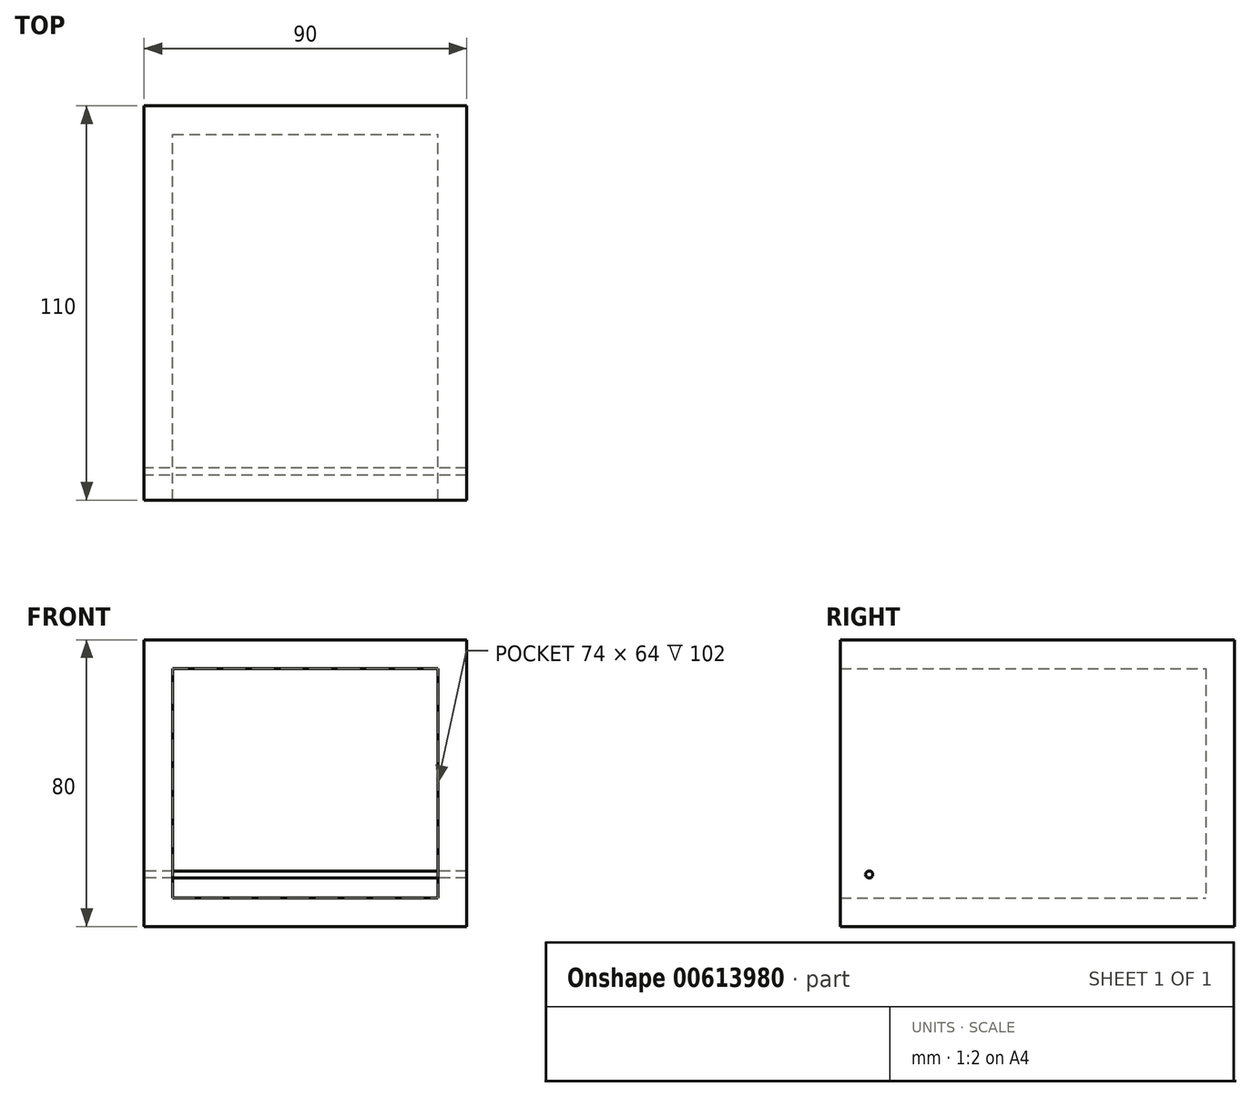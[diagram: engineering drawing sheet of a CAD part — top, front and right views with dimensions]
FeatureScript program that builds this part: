
annotation { "Feature Type Name" : "Feature", "Feature Type Description" : "" }
export const myFeature = defineFeature(function(context is Context, id is Id, definition is map)
    precondition{}
    {
        {
            var Q0;
            Q0=qCreatedBy(makeId("Top.planeOp"),FACE);
            var sketch = newSketch(context, id + "F0", { "sketchPlane" : qUnion([Q0])});
            skPoint(sketch, "E0", {"position": v(-35, 0) * mm});
            skPoint(sketch, "E1", {"position": v(-35, -40.17) * mm});
            skPoint(sketch, "E2", {"position": v(0, -40.17) * mm});
            skPoint(sketch, "E3", {"position": v(0, 61.83) * mm});
            skPoint(sketch, "E4", {"position": v(45, 61.83) * mm});
            skLineSegment(sketch, "E5", {"start": v(45, 61.83) * mm, "end": v(0, 61.83) * mm});
            skLineSegment(sketch, "E6", {"start": v(0, -40.17) * mm, "end": v(45, -40.17) * mm});
            skPoint(sketch, "E7", {"position": v(0, -48.17) * mm});
            skLineSegment(sketch, "E8", {"start": v(0, -48.17) * mm, "end": v(45, -48.17) * mm});
            skLineSegment(sketch, "E9", {"start": v(45, -48.17) * mm, "end": v(45, 61.83) * mm});
            skPoint(sketch, "E10", {"position": v(0, 55.73) * mm});
            skPoint(sketch, "E11", {"position": v(-45, 41.83) * mm});
            skLineSegment(sketch, "E12.MirrorCS", {"start": v(-45, -48.17) * mm, "end": v(-45, 61.83) * mm});
            skLineSegment(sketch, "E13.MirrorCS", {"start": v(-45, 61.83) * mm, "end": v(0, 61.83) * mm});
            skLineSegment(sketch, "E14.MirrorCS", {"start": v(0, -40.17) * mm, "end": v(-45, -40.17) * mm});
            skLineSegment(sketch, "E15.MirrorCS", {"start": v(0, -48.17) * mm, "end": v(-45, -48.17) * mm});
            skLineSegment(sketch, "E16", {"start": v(0, 61.83) * mm, "end": v(0, -48.17) * mm});
            skSolve(sketch);
        }
        {
            var Q0;
            Q0=makeQuery(id+"F0.imprint","IMPRINT",FACE,{"disambiguationData":[TD([[makeQuery(id+"F0.imprint","IMPRINT",EDGE,{"derivedFrom":sQuery(id+"F0.wireOp",EDGE,"2yOScowH-2bkr-TMic-voUo-hkF0jfRCA1gd.bottom")}),1.0]])]});
            var Q1;
            {var subQ0=sQuery(id+"F0.wireOp",EDGE,"E13.MirrorCS");Q1=makeQuery(id+"F0.imprint","IMPRINT",FACE,{"disambiguationData":[TD([[makeQuery(id+"F0.imprint","IMPRINT",EDGE,{"derivedFrom":subQ0}),-1.0]])]});}
            var Q2;
            {var subQ0=sQuery(id+"F0.wireOp",EDGE,"E5");Q2=makeQuery(id+"F0.imprint","IMPRINT",FACE,{"disambiguationData":[TD([[makeQuery(id+"F0.imprint","IMPRINT",EDGE,{"derivedFrom":subQ0}),1.0]])]});}
            var Q3;
            {var subQ0=sQuery(id+"F0.wireOp",EDGE,"E6");Q3=makeQuery(id+"F0.imprint","IMPRINT",FACE,{"disambiguationData":[TD([[makeQuery(id+"F0.imprint","IMPRINT",EDGE,{"derivedFrom":subQ0}),-1.0]])]});}
            var Q4;
            {var subQ2=sQuery(id+"F0.wireOp",EDGE,"E14.MirrorCS");Q4=makeQuery(id+"F0.imprint","IMPRINT",FACE,{"disambiguationData":[TD([[makeQuery(id+"F0.imprint","IMPRINT",EDGE,{"derivedFrom":subQ2}),1.0]])]});}
            extrude(context, id + "F1", {"entities" : qUnion([Q0, Q1, Q2, Q3, Q4]), "depth" : 80 * mm, "offsetDistance" : 25 * mm});
        }
        {
            var Q0;
            Q0=makeQuery(id+"F1.opExtrude","SWEPT_FACE",FACE,{"disambiguationData":[OSD([sQuery(id+"F0.wireOp",EDGE,"2yOScowH-2bkr-TMic-voUo-hkF0jfRCA1gd.top")])]});
            var Q1;
            Q1=makeQuery(id+"F1.opExtrude","SWEPT_FACE",FACE,{"disambiguationData":[OSD([sQuery(id+"F0.wireOp",EDGE,"t2PSzN47-zNYL-cNRn-m0wd-gv9oddS8GhCT")])]});
            var Q2;
            Q2=makeQuery(id+"F1.opExtrude","SWEPT_FACE",FACE,{"disambiguationData":[OSD([sQuery(id+"F0.wireOp",EDGE,"E8"),sQuery(id+"F0.wireOp",EDGE,"E15.MirrorCS")])]});
            shell(context, id + "F2", {"entities" : qUnion([Q0, Q1, Q2]), "thickness" : 8 * mm});
        }
        {
            var Q0;
            Q0=qCreatedBy(makeId("Right.planeOp"),FACE);
            var sketch = newSketch(context, id + "F3", { "sketchPlane" : qUnion([Q0])});
            skPoint(sketch, "E17", {"position": v(-40.17, 0) * mm});
            skPoint(sketch, "E18", {"position": v(-40.17, 9.77) * mm});
            skSolve(sketch);
        }
        {
            var Q0;
            Q0=sQuery(id+"F3.wireOp",VERTEX,"E18");
            var Q1;
            Q1=sQuery(id+"F3.wireOp",VERTEX,"E17");
            var Q2;
            Q2=sQuery(id+"F0.wireOp",VERTEX,"E1");
            cPlane(context, id + "F4", {"entities" : qUnion([Q0, Q1, Q2]), "cplaneType" : CPlaneType.THREE_POINT, "offset" : 25 * mm, "width" : 150 * mm, "height" : 150 * mm});
        }
        {
            var Q0;
            Q0=qCreatedBy(id+"F4.planeOp",FACE);
            var sketch = newSketch(context, id + "F5", { "sketchPlane" : qUnion([Q0])});
            skPoint(sketch, "E19", {"position": v(0, 13.5) * mm});
            skPoint(sketch, "E20", {"position": v(0, 14.5) * mm});
            skLineSegment(sketch, "E21", {"start": v(0, 13.5) * mm, "end": v(-45, 13.5) * mm});
            skLineSegment(sketch, "E22", {"start": v(0, 14.5) * mm, "end": v(-45, 14.5) * mm});
            skLineSegment(sketch, "E23", {"start": v(-45, 14.5) * mm, "end": v(-45, 13.5) * mm});
            skLineSegment(sketch, "E24", {"start": v(0, 13.5) * mm, "end": v(45, 13.5) * mm});
            skLineSegment(sketch, "E25", {"start": v(0, 14.5) * mm, "end": v(45, 14.5) * mm});
            skLineSegment(sketch, "E26", {"start": v(45, 13.5) * mm, "end": v(45, 14.5) * mm});
            skSolve(sketch);
        }
        {
            var Q0;
            Q0=makeQuery(id+"F5.imprint","IMPRINT",FACE,{"disambiguationData":[TD([[makeQuery(id+"F5.imprint","IMPRINT",EDGE,{"derivedFrom":sQuery(id+"F5.wireOp",EDGE,"qvKLtxOb-pAwn-If35-fAg6-ESpUaOsRuz1V")}),1.0]])]});
            var Q1;
            Q1=makeQuery(id+"F5.imprint","IMPRINT",FACE,{"disambiguationData":[TD([[makeQuery(id+"F5.imprint","IMPRINT",EDGE,{"derivedFrom":sQuery(id+"F5.wireOp",EDGE,"E21")}),-1.0]])]});
            var Q2;
            Q2=sQuery(id+"F5.wireOp",EDGE,"E25");
            revolve(context, id + "F6", {"entities" : qUnion([Q0, Q1]), "axis" : qUnion([Q2]), "revolveType" : RevolveType.FULL});
        }
    });
